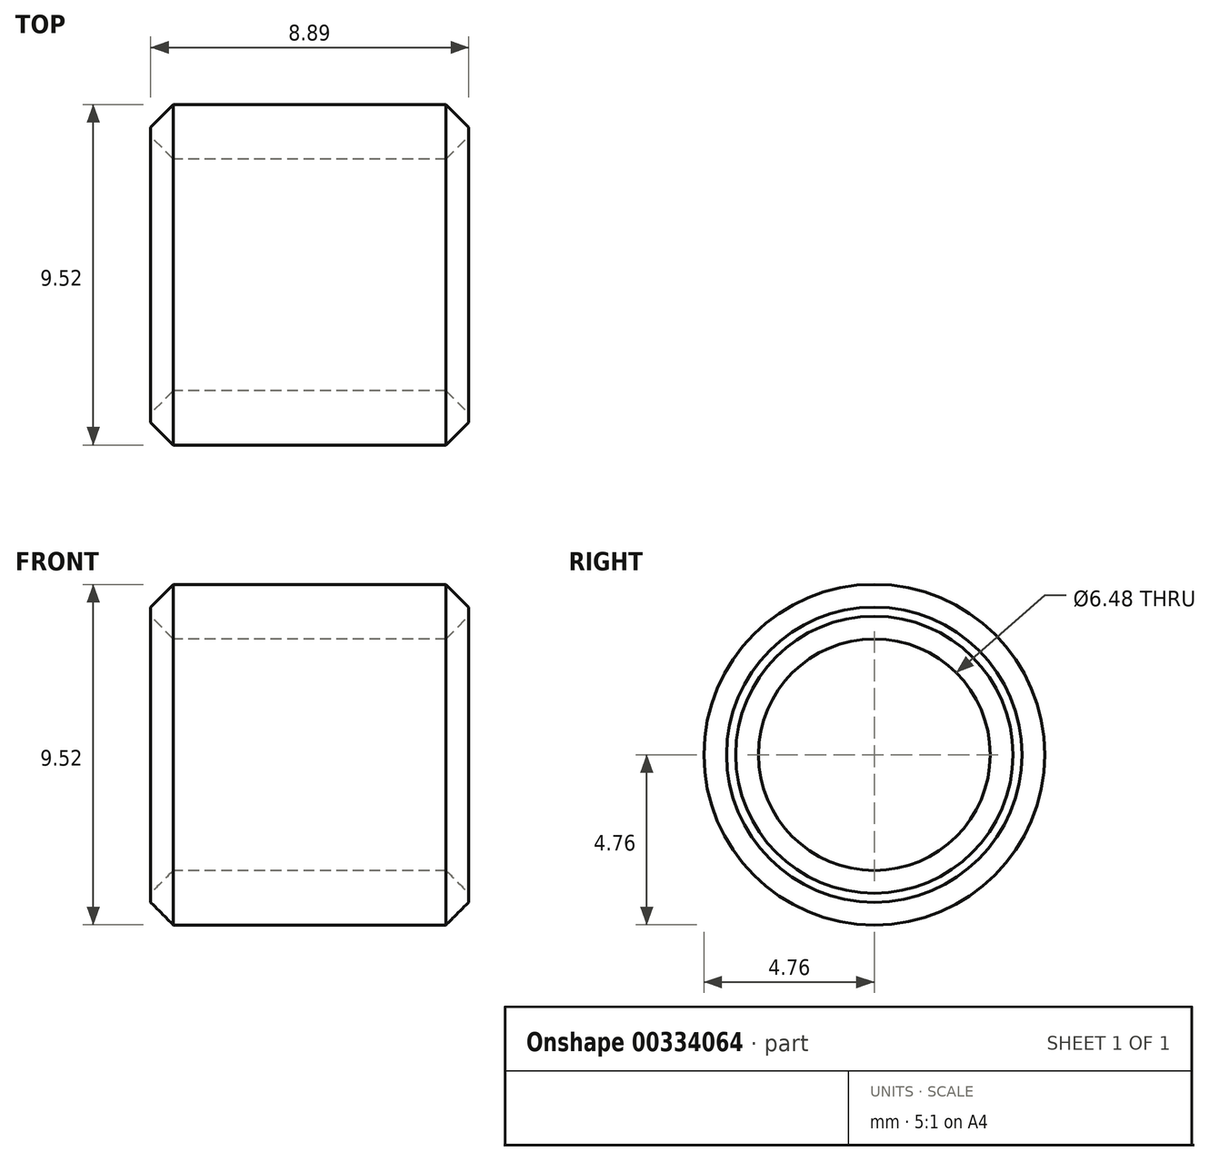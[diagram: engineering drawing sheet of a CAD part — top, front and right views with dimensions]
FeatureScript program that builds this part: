
annotation { "Feature Type Name" : "Feature", "Feature Type Description" : "" }
export const myFeature = defineFeature(function(context is Context, id is Id, definition is map)
    precondition{}
    {
        {
            var Q0;
            Q0=qCreatedBy(makeId("Right.planeOp"),FACE);
            var sketch = newSketch(context, id + "F0", { "sketchPlane" : qUnion([Q0])});
            skCircle(sketch, "E0", {"center": v(0, 0) * mm, "radius": 3.24 * mm});
            skCircle(sketch, "E1", {"center": v(0, 0) * mm, "radius": 4.76 * mm});
            skSolve(sketch);
        }
        {
            var Q0;
            Q0=makeQuery(id+"F0.imprint","IMPRINT",FACE,{"disambiguationData":[TD([[makeQuery(id+"F0.imprint","IMPRINT",EDGE,{"derivedFrom":sQuery(id+"F0.wireOp",EDGE,"E0")}),-1.0]])]});
            extrude(context, id + "F1", {"entities" : qUnion([Q0]), "depth" : 8.9 * mm});
        }
        {
            var Q0;
            Q0=makeQuery(id+"F1.opExtrude","CAP_EDGE",EDGE,{"disambiguationData":[OSD([sQuery(id+"F0.wireOp",EDGE,"E0")])],"isStart":false});
            var Q1;
            Q1=makeQuery(id+"F1.opExtrude","CAP_EDGE",EDGE,{"disambiguationData":[OSD([sQuery(id+"F0.wireOp",EDGE,"E1")])],"isStart":false});
            var Q2;
            Q2=makeQuery(id+"F1.opExtrude","CAP_EDGE",EDGE,{"disambiguationData":[OSD([sQuery(id+"F0.wireOp",EDGE,"E0")])],"isStart":true});
            var Q3;
            Q3=makeQuery(id+"F1.opExtrude","CAP_FACE",FACE,{"disambiguationData":[OSD([sQuery(id+"F0.wireOp",EDGE,"E0"),sQuery(id+"F0.wireOp",EDGE,"E1")])],"isStart":true});
            chamfer(context, id + "F2", {"entities" : qUnion([Q0, Q1, Q2, Q3]), "width" : 0.64 * mm, "tangentPropagation" : true});
        }
    });
